# Revit family: SLSX4x4
name_source: partatom
category: Lighting Fixtures
units: mm (PartAtom-declared; Revit-internal decimal feet)

## family parameters
Always vertical = Yes
Cut with Voids When Loaded = No
Host = Ceiling
Light Source = Yes
Maintain Annotation Orientation = No
OmniClass Number = 23.80.70.11.14.17
OmniClass Title = Direct/Indirect
Part Type = Normal
Room Calculation Point = No
Round Connector Dimension = Use Diameter
Shared = No

## types (5) — shared parameters
Assembly Code = D5020200
Color Filter = 16777215
Default Elevation = 0' - 0"
Description = Architectural Pendant with Convex lens
Dimming Lamp Color Temperature Shift = <None>
Emit Shape Visible in Rendering = No
Emit from Rectangle Height = 0' - 5 13/32"
Emit from Rectangle Length = 3' - 9 5/8"
Emit from Rectangle Width = 3' - 9 5/8"
Housing Finish = Metal - Viscor - White
Lamp = LED
Length = 3' - 9 5/8"
Lens Depth = 0' - 5 13/32"
Lens Finish = Acrylic - Viscor - Opal White Square
Manufacturer = VISIONEERING by VISCOR
Model = SLSX4x4
Tilt Angle = 90.00°
URL = https://viscor.com
Voltage = 120 V
Width = 3' - 9 5/8"

## per-type parameters (varying)
| type | Apparent Load | Lamp Wattage | Photometric Web File |
| SLSX4X4-LED840L080LUNV | 61 VA | 61 VA | SLSX4X4-LED840K080LUNV.ies |
| SLSV4X4-LED840K100LUNV | 84 VA | 84 VA | SLSX4X4-LED840K100LUNV.ies |
| SLSV4X4-LED840K120LUNV | 94 VA | 94 VA | SLSX4X4-LED840K120LUNV.ies |
| SLSV4X4-LED840K140LUNV | 111 VA | 111 VA | SLSX4X4-LED840K140LUNV.ies |
| SLSV4X4-LED840K160LUNV | 128 VA | 128 VA | SLSX4X4-LED840K160LUNV.ies |

## geometry (parser evidence)
native form markers: Sweep x3
no freeform markers — native parametric forms only
